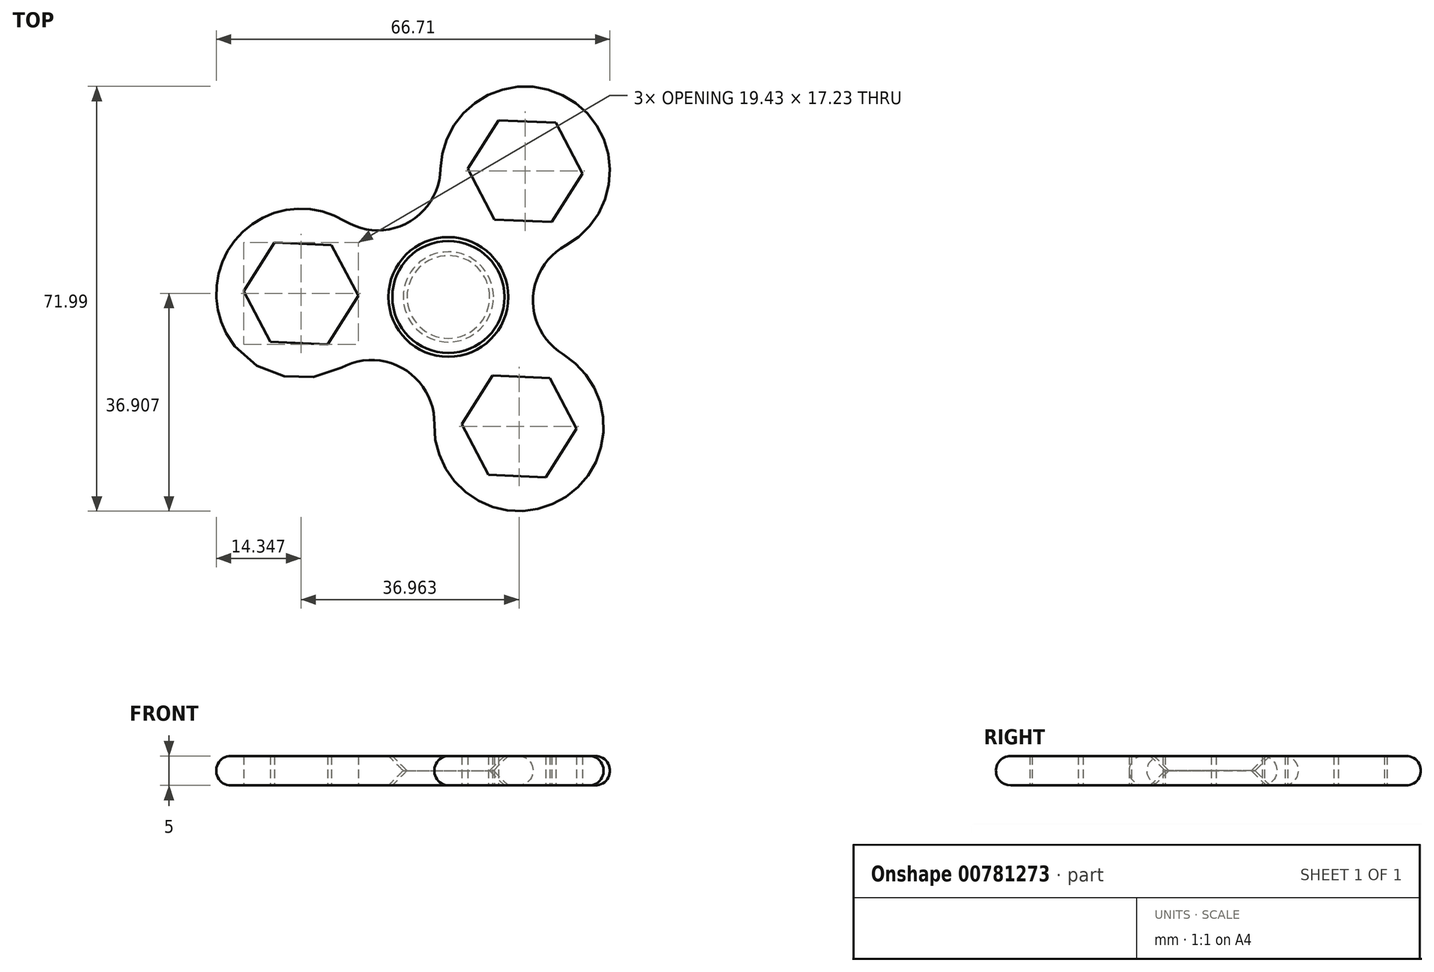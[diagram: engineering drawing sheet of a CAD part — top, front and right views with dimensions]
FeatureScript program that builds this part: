
annotation { "Feature Type Name" : "Feature", "Feature Type Description" : "" }
export const myFeature = defineFeature(function(context is Context, id is Id, definition is map)
    precondition{}
    {
        {
            var Q0;
            Q0=qCreatedBy(makeId("Top.planeOp"),FACE);
            var sketch = newSketch(context, id + "F0", { "sketchPlane" : qUnion([Q0])});
            skCircle(sketch, "E0", {"center": v(0, 0) * mm, "radius": 14.35 * mm});
            skCircle(sketch, "E1.cCircle", {"center": v(-25, 0.6) * mm, "radius": 8.42 * mm, "construction": true});
            skLineSegment(sketch, "E1.0", {"start": v(-15.28, 0.2) * mm, "end": v(-20.48, -8) * mm});
            skLineSegment(sketch, "E1.1", {"start": v(-20.48, -8) * mm, "end": v(-30.2, -7.6) * mm});
            skLineSegment(sketch, "E1.2", {"start": v(-30.2, -7.6) * mm, "end": v(-34.7, 1) * mm});
            skLineSegment(sketch, "E1.3", {"start": v(-34.7, 1) * mm, "end": v(-29.5, 9.22) * mm});
            skLineSegment(sketch, "E1.4", {"start": v(-29.5, 9.22) * mm, "end": v(-19.79, 8.82) * mm});
            skLineSegment(sketch, "E1.5", {"start": v(-19.79, 8.82) * mm, "end": v(-15.28, 0.2) * mm});
            skPoint(sketch, "E1.0.midPoint", {"position": v(-17.88, -3.9) * mm});
            skArc(sketch, "E2", {"start": v(-17.52, 12.86) * mm, "mid": v(-39.34, 0.96) * mm, "end": v(-18.12, -12) * mm});
            skLineSegment(sketch, "E3.1.0", {"start": v(17.17, -13.73) * mm, "end": v(21.68, -22.35) * mm});
            skLineSegment(sketch, "E3.1.1", {"start": v(16.48, -30.56) * mm, "end": v(6.77, -30.16) * mm});
            skArc(sketch, "E3.1.2", {"start": v(12.32, -7.6) * mm, "mid": v(12.25, -7.6) * mm, "end": v(12.17, -7.6) * mm});
            skLineSegment(sketch, "E3.1.3", {"start": v(6.77, -30.16) * mm, "end": v(2.26, -21.55) * mm});
            skCircle(sketch, "E3.1.4", {"center": v(11.97, -21.95) * mm, "radius": 8.42 * mm, "construction": true});
            skPoint(sketch, "E3.1.5", {"position": v(12.32, -13.53) * mm});
            skLineSegment(sketch, "E3.1.6", {"start": v(7.46, -13.34) * mm, "end": v(17.17, -13.73) * mm});
            skLineSegment(sketch, "E3.1.7", {"start": v(21.68, -22.35) * mm, "end": v(16.48, -30.56) * mm});
            skLineSegment(sketch, "E3.1.8", {"start": v(2.26, -21.55) * mm, "end": v(7.46, -13.34) * mm});
            skLineSegment(sketch, "E3.2.0", {"start": v(3.3, 21.74) * mm, "end": v(8.51, 29.95) * mm});
            skLineSegment(sketch, "E3.2.1", {"start": v(18.23, 29.55) * mm, "end": v(22.74, 20.94) * mm});
            skArc(sketch, "E3.2.2", {"start": v(12.53, 7) * mm, "mid": v(12.6, 7) * mm, "end": v(12.67, 7) * mm});
            skLineSegment(sketch, "E3.2.3", {"start": v(22.74, 20.94) * mm, "end": v(17.53, 12.73) * mm});
            skCircle(sketch, "E3.2.4", {"center": v(13.02, 21.34) * mm, "radius": 8.42 * mm, "construction": true});
            skPoint(sketch, "E3.2.5", {"position": v(5.56, 17.43) * mm});
            skLineSegment(sketch, "E3.2.6", {"start": v(7.82, 13.13) * mm, "end": v(3.3, 21.74) * mm});
            skLineSegment(sketch, "E3.2.7", {"start": v(8.51, 29.95) * mm, "end": v(18.23, 29.55) * mm});
            skLineSegment(sketch, "E3.2.8", {"start": v(17.53, 12.73) * mm, "end": v(7.82, 13.13) * mm});
            skLineSegment(sketch, "E4", {"start": v(-25, 0.6) * mm, "end": v(13.02, 21.34) * mm, "construction": true});
            skLineSegment(sketch, "E5", {"start": v(13.02, 21.34) * mm, "end": v(11.97, -21.95) * mm, "construction": true});
            skLineSegment(sketch, "E6", {"start": v(-25, 0.6) * mm, "end": v(11.97, -21.95) * mm, "construction": true});
            skArc(sketch, "E7", {"start": v(-17.52, 12.86) * mm, "mid": v(-6.87, 12.6) * mm, "end": v(-1.32, 21.69) * mm});
            skArc(sketch, "E8.1.0", {"start": v(-2.38, -21.6) * mm, "mid": v(-7.47, -12.25) * mm, "end": v(-18.12, -12) * mm});
            skArc(sketch, "E8.2.0", {"start": v(19.9, 8.74) * mm, "mid": v(14.35, -0.35) * mm, "end": v(19.45, -9.7) * mm});
            skArc(sketch, "E9.trimOffspring", {"start": v(-12.33, 7.35) * mm, "mid": v(-12.36, 7.41) * mm, "end": v(-12.4, 7.48) * mm});
            skArc(sketch, "E10.trimOffspring", {"start": v(-12.74, -6.87) * mm, "mid": v(-12.7, -6.8) * mm, "end": v(-12.67, -6.74) * mm});
            skArc(sketch, "E11.trimOffspring", {"start": v(0.42, 14.47) * mm, "mid": v(0.46, 14.4) * mm, "end": v(0.5, 14.34) * mm});
            skArc(sketch, "E12.trimOffspring", {"start": v(19.9, 8.74) * mm, "mid": v(20.5, 33.6) * mm, "end": v(-1.32, 21.69) * mm});
            skArc(sketch, "E13.trimOffspring", {"start": v(-0.2, -14.35) * mm, "mid": v(-0.24, -14.41) * mm, "end": v(-0.28, -14.47) * mm});
            skArc(sketch, "E14.trimOffspring", {"start": v(-2.38, -21.6) * mm, "mid": v(18.84, -34.55) * mm, "end": v(19.45, -9.7) * mm});
            skSolve(sketch);
        }
        {
            var Q0;
            Q0 = qSketchRegion(id + "F0", true);
            extrude(context, id + "F1", {"entities" : qUnion([Q0]), "depth" : 5 * mm, "offsetDistance" : 25 * mm});
        }
        {
            var Q0;
            Q0=makeQuery(id+"F1.opExtrude","CAP_EDGE",EDGE,{"disambiguationData":[OSD([sQuery(id+"F0.wireOp",EDGE,"E8.1.0")])],"isStart":false});
            var Q1;
            Q1=makeQuery(id+"F1.opExtrude","CAP_EDGE",EDGE,{"disambiguationData":[OSD([sQuery(id+"F0.wireOp",EDGE,"E14.trimOffspring")])],"isStart":true});
            fillet(context, id + "F2", {"entities" : qUnion([Q0, Q1]), "radius" : 2.5 * mm, "tangentPropagation" : true, "allowEdgeOverflow" : false});
        }
        {
            var Q0;
            Q0=qCreatedBy(makeId("Right.planeOp"),FACE);
            var sketch = newSketch(context, id + "F3", { "sketchPlane" : qUnion([Q0])});
            skLineSegment(sketch, "E15.0", {"start": v(-11.83, 5) * mm, "end": v(10.94, 5) * mm});
            skLineSegment(sketch, "E16.0", {"start": v(10.94, 0) * mm, "end": v(-11.83, 0) * mm});
            skLineSegment(sketch, "E17", {"start": v(0, 0) * mm, "end": v(0, 5) * mm, "construction": true});
            skLineSegment(sketch, "E18", {"start": v(9.5, 5) * mm, "end": v(7, 2.5) * mm});
            skLineSegment(sketch, "E19", {"start": v(7, 2.5) * mm, "end": v(9.5, 0) * mm});
            skLineSegment(sketch, "E20", {"start": v(10.15, 5) * mm, "end": v(9.5, 5) * mm});
            skPoint(sketch, "E21", {"position": v(0, 2.5) * mm});
            skPoint(sketch, "E22", {"position": v(7.05, 9.49) * mm});
            skLineSegment(sketch, "E23", {"start": v(10.15, 5) * mm, "end": v(7.65, 2.5) * mm});
            skLineSegment(sketch, "E24", {"start": v(7.65, 2.5) * mm, "end": v(10.15, 0) * mm});
            skSolve(sketch);
        }
        {
            var Q0;
            Q0 = qSketchRegion(id + "F3", true);
            var Q1;
            Q1=sQuery(id+"F3.wireOp",EDGE,"E17");
            revolve(context, id + "F4", {"operationType" : NewBodyOperationType.REMOVE, "surfaceOperationType" : NewSurfaceOperationType.NEW, "entities" : qUnion([Q0]), "axis" : qUnion([Q1]), "revolveType" : RevolveType.FULL});
        }
    });
